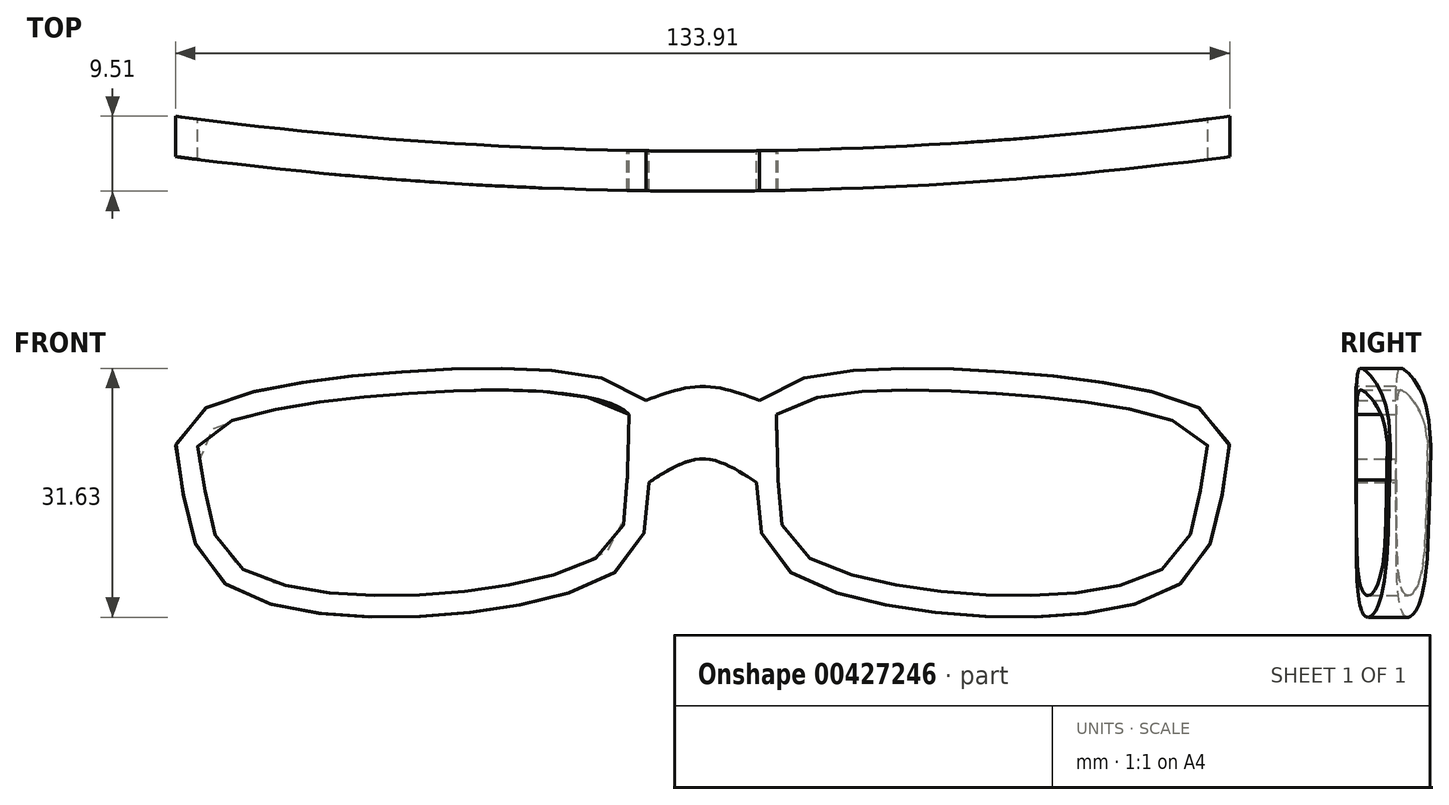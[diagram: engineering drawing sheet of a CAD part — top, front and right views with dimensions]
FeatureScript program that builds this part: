
annotation { "Feature Type Name" : "Feature", "Feature Type Description" : "" }
export const myFeature = defineFeature(function(context is Context, id is Id, definition is map)
    precondition{}
    {
        {
            var Q0;
            Q0=qCreatedBy(makeId("Front.planeOp"),FACE);
            var sketch = newSketch(context, id + "F0", { "sketchPlane" : qUnion([Q0])});
            skFitSpline(sketch, "E0", {"points": [v(-85.04, 21.14) * mm, v(-85.04, 29.55) * mm, v(-57.42, 36.35) * mm, v(-26.2, 32.75) * mm, v(-25.8, 22.34) * mm, v(-29.8, 11.13) * mm, v(-77.83, 8.33) * mm, v(-85.04, 21.14) * mm]});
            skLineSegment(sketch, "E1", {"start": v(-19, 51.16) * mm, "end": v(-19, -19.28) * mm, "construction": true});
            skFitSpline(sketch, "E2.MirrorC", {"points": [v(47.04, 21.14) * mm, v(47.04, 29.55) * mm, v(19.43, 36.35) * mm, v(-11.8, 32.75) * mm, v(-12.2, 22.34) * mm, v(-8.19, 11.13) * mm, v(39.84, 8.33) * mm, v(47.04, 21.14) * mm]});
            skFitSpline(sketch, "E3", {"points": [v(-26.2, 32.75) * mm, v(-19, 34.53) * mm, v(-11.8, 32.75) * mm], "startDerivative": vector(14.4, 5.34) * mm, "endDerivative": vector(14.4, -5.34) * mm});
            skFitSpline(sketch, "E4", {"points": [v(-25.8, 22.34) * mm, v(-19, 25.32) * mm, v(-12.2, 22.34) * mm], "startDerivative": vector(13.6, 8.94) * mm, "endDerivative": vector(13.6, -8.94) * mm});
            skSolve(sketch);
        }
        {
            var Q0;
            {var subQ0=sQuery(id+"F0.wireOp",EDGE,"E0");var subQ1=makeQuery(id+"F0.imprint","INTERSECT",VERTEX,{"derivedFrom":[subQ0,sQuery(id+"F0.wireOp",EDGE,"E3")]});Q0=makeQuery(id+"F0.imprint","IMPRINT",FACE,{"disambiguationData":[TD([[makeQuery(id+"F0.imprint","IMPRINT",EDGE,{"disambiguationData":[TD([[subQ1,-1.0]])],"derivedFrom":subQ0}),-1.0]])]});}
            var Q1;
            {var subQ0=sQuery(id+"F0.wireOp",EDGE,"E3");Q1=makeQuery(id+"F0.imprint","IMPRINT",FACE,{"disambiguationData":[TD([[makeQuery(id+"F0.imprint","IMPRINT",EDGE,{"derivedFrom":subQ0}),-1.0]])]});}
            var Q2;
            {var subQ0=sQuery(id+"F0.wireOp",EDGE,"E2.MirrorC");var subQ1=makeQuery(id+"F0.imprint","INTERSECT",VERTEX,{"derivedFrom":[subQ0,sQuery(id+"F0.wireOp",EDGE,"E3")]});Q2=makeQuery(id+"F0.imprint","IMPRINT",FACE,{"disambiguationData":[TD([[makeQuery(id+"F0.imprint","IMPRINT",EDGE,{"disambiguationData":[TD([[subQ1,-1.0]])],"derivedFrom":subQ0}),1.0]])]});}
            extrude(context, id + "F1", {"entities" : qUnion([Q0, Q1, Q2]), "depth" : 50.8 * mm});
        }
        {
            var Q0;
            Q0=qCreatedBy(makeId("Top.planeOp"),FACE);
            var sketch = newSketch(context, id + "F2", { "sketchPlane" : qUnion([Q0])});
            skPoint(sketch, "E5.0", {"position": v(-19, 0) * mm});
            skLineSegment(sketch, "E6", {"start": v(-85.95, -425) * mm, "end": v(-85.95, -30.52) * mm, "construction": true});
            skLineSegment(sketch, "E7", {"start": v(47.95, 0) * mm, "end": v(47.95, -25.4) * mm, "construction": true});
            skArc(sketch, "E8", {"start": v(-85.95, -25.4) * mm, "mid": v(-19, -29.83) * mm, "end": v(47.95, -25.4) * mm});
            skArc(sketch, "E9.0", {"start": v(-85.95, -30.52) * mm, "mid": v(-19, -34.91) * mm, "end": v(47.95, -30.52) * mm});
            skLineSegment(sketch, "E10", {"start": v(-85.95, -50.8) * mm, "end": v(-85.95, -30.52) * mm});
            skLineSegment(sketch, "E11", {"start": v(47.95, 0) * mm, "end": v(47.95, -25.4) * mm});
            skLineSegment(sketch, "E12", {"start": v(-85.95, -50.8) * mm, "end": v(47.95, -50.8) * mm});
            skLineSegment(sketch, "E13", {"start": v(47.95, 0) * mm, "end": v(-85.95, 0) * mm});
            skLineSegment(sketch, "E14.trimOffspring", {"start": v(47.95, -30.52) * mm, "end": v(47.95, -50.8) * mm, "construction": true});
            skLineSegment(sketch, "E15.trimOffspring", {"start": v(47.95, -30.52) * mm, "end": v(47.95, -50.8) * mm});
            skLineSegment(sketch, "E16.trimOffspring", {"start": v(-85.95, -25.4) * mm, "end": v(-85.95, 374.2) * mm, "construction": true});
            skLineSegment(sketch, "E17.trimOffspring", {"start": v(-85.95, -25.4) * mm, "end": v(-85.95, 0) * mm});
            skSolve(sketch);
        }
        {
            var Q0;
            Q0 = qSketchRegion(id + "F2", true);
            extrude(context, id + "F3", {"entities" : qUnion([Q0]), "operationType" : NewBodyOperationType.REMOVE, "depth" : 127 * mm});
        }
        {
            var Q0;
            Q0=qCreatedBy(makeId("Front.planeOp"),FACE);
            var sketch = newSketch(context, id + "F4", { "sketchPlane" : qUnion([Q0])});
            skFitSpline(sketch, "E18.0.0", {"points": [v(-26.2, 32.75) * mm, v(-26.45, 33.05) * mm, v(-27.02, 33.57) * mm, v(-27.83, 34.1) * mm, v(-28.52, 34.46) * mm, v(-29.22, 34.78) * mm, v(-30.12, 35.12) * mm, v(-31.22, 35.45) * mm, v(-32.34, 35.73) * mm, v(-33.47, 35.96) * mm, v(-34.99, 36.22) * mm, v(-36.89, 36.46) * mm, v(-39.93, 36.71) * mm, v(-43.73, 36.85) * mm, v(-48.3, 36.82) * mm, v(-52.88, 36.64) * mm, v(-57.45, 36.36) * mm, v(-62, 36) * mm, v(-65.8, 35.6) * mm, v(-68.8, 35.2) * mm, v(-71.06, 34.86) * mm, v(-73.31, 34.46) * mm, v(-75.55, 33.98) * mm, v(-77.76, 33.42) * mm, v(-79.57, 32.85) * mm, v(-80.99, 32.3) * mm, v(-82.04, 31.83) * mm, v(-83.05, 31.28) * mm, v(-83.83, 30.74) * mm, v(-84.42, 30.24) * mm, v(-84.83, 29.82) * mm, v(-85.18, 29.37) * mm, v(-85.47, 28.86) * mm, v(-85.7, 28.33) * mm, v(-85.84, 27.77) * mm, v(-85.93, 27.2) * mm, v(-85.96, 26.43) * mm, v(-85.9, 25.47) * mm, v(-85.71, 24.32) * mm, v(-85.48, 23.19) * mm, v(-85.23, 22.06) * mm, v(-84.99, 20.93) * mm, v(-84.78, 19.8) * mm, v(-84.56, 18.65) * mm, v(-84.25, 17.14) * mm, v(-83.87, 15.65) * mm, v(-83.32, 14.19) * mm, v(-82.83, 13.14) * mm, v(-82.25, 12.16) * mm, v(-81.56, 11.23) * mm, v(-80.77, 10.37) * mm, v(-79.9, 9.62) * mm, v(-78.96, 8.96) * mm, v(-77.96, 8.38) * mm, v(-76.91, 7.89) * mm, v(-75.84, 7.46) * mm, v(-74.76, 7.1) * mm, v(-73.3, 6.68) * mm, v(-71.44, 6.25) * mm, v(-69.55, 5.93) * mm, v(-68.03, 5.72) * mm, v(-65.75, 5.46) * mm, v(-62.33, 5.22) * mm, v(-57.79, 5.17) * mm, v(-53.24, 5.34) * mm, v(-48.7, 5.73) * mm, v(-44.93, 6.25) * mm, v(-41.9, 6.8) * mm, v(-39.65, 7.28) * mm, v(-37.42, 7.85) * mm, v(-35.21, 8.53) * mm, v(-33.42, 9.2) * mm, v(-32.03, 9.83) * mm, v(-31.01, 10.36) * mm, v(-30.19, 10.86) * mm, v(-29.55, 11.31) * mm, v(-28.95, 11.79) * mm, v(-28.4, 12.32) * mm, v(-27.9, 12.9) * mm, v(-27.56, 13.38) * mm, v(-27.25, 13.87) * mm, v(-26.9, 14.55) * mm, v(-26.56, 15.44) * mm, v(-26.28, 16.58) * mm, v(-26.06, 18.1) * mm, v(-25.95, 20.03) * mm, v(-25.88, 21.57) * mm, v(-25.8, 22.34) * mm]});
            skFitSpline(sketch, "E18.0.1", {"points": [v(-25.8, 22.34) * mm, v(-25.28, 22.68) * mm, v(-24.23, 23.37) * mm, v(-22.89, 24.16) * mm, v(-21.9, 24.63) * mm, v(-21.32, 24.86) * mm, v(-20.72, 25.07) * mm, v(-19.96, 25.26) * mm, v(-19.18, 25.33) * mm, v(-18.54, 25.3) * mm, v(-17.92, 25.23) * mm, v(-17.16, 25.04) * mm, v(-16.26, 24.71) * mm, v(-15.12, 24.17) * mm, v(-13.77, 23.38) * mm, v(-12.72, 22.69) * mm, v(-12.2, 22.34) * mm]});
            skFitSpline(sketch, "E18.0.2", {"points": [v(-12.2, 22.34) * mm, v(-12.12, 21.57) * mm, v(-12.04, 20.03) * mm, v(-11.94, 18.1) * mm, v(-11.71, 16.58) * mm, v(-11.44, 15.44) * mm, v(-11.1, 14.55) * mm, v(-10.74, 13.87) * mm, v(-10.44, 13.38) * mm, v(-10.1, 12.9) * mm, v(-9.6, 12.32) * mm, v(-9.04, 11.79) * mm, v(-8.44, 11.31) * mm, v(-7.8, 10.86) * mm, v(-6.98, 10.36) * mm, v(-5.96, 9.83) * mm, v(-4.57, 9.2) * mm, v(-2.78, 8.53) * mm, v(-0.57, 7.85) * mm, v(1.66, 7.28) * mm, v(3.91, 6.8) * mm, v(6.94, 6.25) * mm, v(10.71, 5.73) * mm, v(15.25, 5.34) * mm, v(19.8, 5.17) * mm, v(24.34, 5.22) * mm, v(27.76, 5.46) * mm, v(30.04, 5.72) * mm, v(31.56, 5.93) * mm, v(33.44, 6.25) * mm, v(35.3, 6.68) * mm, v(36.77, 7.1) * mm, v(37.85, 7.46) * mm, v(38.92, 7.89) * mm, v(39.97, 8.38) * mm, v(40.97, 8.96) * mm, v(41.9, 9.62) * mm, v(42.77, 10.37) * mm, v(43.57, 11.23) * mm, v(44.26, 12.16) * mm, v(44.84, 13.14) * mm, v(45.33, 14.19) * mm, v(45.87, 15.65) * mm, v(46.26, 17.14) * mm, v(46.57, 18.65) * mm, v(46.78, 19.8) * mm, v(47, 20.93) * mm, v(47.24, 22.06) * mm, v(47.49, 23.19) * mm, v(47.72, 24.32) * mm, v(47.9, 25.47) * mm, v(47.97, 26.43) * mm, v(47.93, 27.2) * mm, v(47.85, 27.77) * mm, v(47.7, 28.33) * mm, v(47.48, 28.86) * mm, v(47.18, 29.37) * mm, v(46.83, 29.82) * mm, v(46.43, 30.24) * mm, v(45.84, 30.74) * mm, v(45.05, 31.28) * mm, v(44.04, 31.83) * mm, v(43, 32.3) * mm, v(41.58, 32.85) * mm, v(39.77, 33.42) * mm, v(37.56, 33.98) * mm, v(35.32, 34.46) * mm, v(33.07, 34.86) * mm, v(30.82, 35.2) * mm, v(27.8, 35.6) * mm, v(24.01, 36) * mm, v(19.46, 36.36) * mm, v(14.89, 36.64) * mm, v(10.31, 36.82) * mm, v(5.74, 36.85) * mm, v(1.94, 36.71) * mm, v(-1.1, 36.46) * mm, v(-3, 36.22) * mm, v(-4.52, 35.96) * mm, v(-5.66, 35.73) * mm, v(-6.77, 35.45) * mm, v(-7.87, 35.12) * mm, v(-8.77, 34.78) * mm, v(-9.47, 34.46) * mm, v(-10.16, 34.1) * mm, v(-10.97, 33.57) * mm, v(-11.54, 33.05) * mm, v(-11.8, 32.75) * mm]});
            skFitSpline(sketch, "E18.0.3", {"points": [v(-11.8, 32.75) * mm, v(-12.38, 32.96) * mm, v(-13.55, 33.4) * mm, v(-15.32, 33.98) * mm, v(-17.15, 34.4) * mm, v(-18.68, 34.56) * mm, v(-19.92, 34.5) * mm, v(-21.17, 34.33) * mm, v(-22.68, 33.97) * mm, v(-24.45, 33.4) * mm, v(-25.62, 32.96) * mm, v(-26.2, 32.75) * mm]});
            skFitSpline(sketch, "E19.0", {"points": [v(-9.41, 22.62) * mm, v(-9.33, 21.76) * mm, v(-9.25, 20.13) * mm, v(-9.15, 18.34) * mm, v(-8.96, 17.1) * mm, v(-8.76, 16.27) * mm, v(-8.49, 15.56) * mm, v(-8.19, 15.04) * mm, v(-7.9, 14.64) * mm, v(-7.57, 14.26) * mm, v(-7.2, 13.9) * mm, v(-6.76, 13.55) * mm, v(-6.28, 13.2) * mm, v(-5.62, 12.8) * mm, v(-4.75, 12.35) * mm, v(-3.52, 11.8) * mm, v(-1.88, 11.18) * mm, v(0.18, 10.55) * mm, v(3, 9.82) * mm, v(6.63, 9.11) * mm, v(11.02, 8.51) * mm, v(15.43, 8.13) * mm, v(19.83, 7.96) * mm, v(24.24, 8.01) * mm, v(27.88, 8.26) * mm, v(30.77, 8.63) * mm, v(32.9, 9) * mm, v(34.96, 9.47) * mm, v(36.6, 9.97) * mm, v(37.66, 10.4) * mm, v(38.25, 10.66) * mm, v(38.81, 10.94) * mm, v(39.47, 11.32) * mm, v(40.18, 11.83) * mm, v(40.83, 12.38) * mm, v(41.42, 13.02) * mm, v(41.92, 13.7) * mm, v(42.36, 14.45) * mm, v(42.75, 15.26) * mm, v(43.2, 16.46) * mm, v(43.54, 17.77) * mm, v(43.8, 19) * mm, v(43.93, 19.74) * mm, v(44.04, 20.3) * mm, v(44.14, 20.88) * mm, v(44.26, 21.47) * mm, v(44.38, 22.07) * mm, v(44.55, 22.85) * mm, v(44.76, 23.79) * mm, v(44.98, 24.84) * mm, v(45.13, 25.8) * mm, v(45.17, 26.5) * mm, v(45.15, 26.93) * mm, v(45.1, 27.22) * mm, v(45.05, 27.4) * mm, v(45, 27.53) * mm, v(44.95, 27.65) * mm, v(44.88, 27.77) * mm, v(44.8, 27.89) * mm, v(44.7, 28.01) * mm, v(44.52, 28.2) * mm, v(44.17, 28.5) * mm, v(43.61, 28.88) * mm, v(42.8, 29.32) * mm, v(41.92, 29.72) * mm, v(40.67, 30.2) * mm, v(39.01, 30.73) * mm, v(36.93, 31.26) * mm, v(34.8, 31.71) * mm, v(32.62, 32.1) * mm, v(30.43, 32.43) * mm, v(27.48, 32.82) * mm, v(23.76, 33.21) * mm, v(19.26, 33.58) * mm, v(14.74, 33.85) * mm, v(10.25, 34.02) * mm, v(5.77, 34.05) * mm, v(2.09, 33.92) * mm, v(-0.82, 33.68) * mm, v(-2.6, 33.45) * mm, v(-4.01, 33.22) * mm, v(-5.04, 33) * mm, v(-6.03, 32.76) * mm, v(-6.98, 32.47) * mm, v(-7.71, 32.2) * mm, v(-8.25, 31.95) * mm, v(-8.63, 31.75) * mm, v(-8.96, 31.55) * mm, v(-9.25, 31.34) * mm, v(-9.48, 31.14) * mm, v(-9.6, 31.02) * mm, v(-9.65, 30.96) * mm]});
            skFitSpline(sketch, "E20.0", {"points": [v(-28.35, 30.96) * mm, v(-28.4, 31.02) * mm, v(-28.51, 31.14) * mm, v(-28.75, 31.34) * mm, v(-29.03, 31.55) * mm, v(-29.37, 31.75) * mm, v(-29.75, 31.95) * mm, v(-30.28, 32.2) * mm, v(-31.01, 32.47) * mm, v(-31.96, 32.76) * mm, v(-32.95, 33) * mm, v(-33.98, 33.22) * mm, v(-35.39, 33.45) * mm, v(-37.17, 33.68) * mm, v(-40.08, 33.92) * mm, v(-43.77, 34.05) * mm, v(-48.24, 34.02) * mm, v(-52.74, 33.85) * mm, v(-57.25, 33.58) * mm, v(-61.75, 33.21) * mm, v(-65.47, 32.82) * mm, v(-68.42, 32.43) * mm, v(-70.61, 32.1) * mm, v(-72.78, 31.71) * mm, v(-74.93, 31.26) * mm, v(-77, 30.73) * mm, v(-78.66, 30.2) * mm, v(-79.91, 29.72) * mm, v(-80.8, 29.32) * mm, v(-81.6, 28.88) * mm, v(-82.16, 28.5) * mm, v(-82.51, 28.2) * mm, v(-82.69, 28.01) * mm, v(-82.79, 27.89) * mm, v(-82.87, 27.77) * mm, v(-82.94, 27.65) * mm, v(-83, 27.53) * mm, v(-83.05, 27.4) * mm, v(-83.1, 27.22) * mm, v(-83.14, 26.93) * mm, v(-83.16, 26.5) * mm, v(-83.12, 25.8) * mm, v(-82.97, 24.84) * mm, v(-82.75, 23.79) * mm, v(-82.54, 22.85) * mm, v(-82.37, 22.07) * mm, v(-82.25, 21.47) * mm, v(-82.14, 20.88) * mm, v(-82.03, 20.3) * mm, v(-81.92, 19.74) * mm, v(-81.78, 19) * mm, v(-81.53, 17.77) * mm, v(-81.19, 16.46) * mm, v(-80.74, 15.26) * mm, v(-80.36, 14.45) * mm, v(-79.91, 13.7) * mm, v(-79.41, 13.02) * mm, v(-78.82, 12.38) * mm, v(-78.18, 11.83) * mm, v(-77.46, 11.32) * mm, v(-76.8, 10.94) * mm, v(-76.24, 10.66) * mm, v(-75.65, 10.4) * mm, v(-74.58, 9.97) * mm, v(-72.95, 9.47) * mm, v(-70.9, 9) * mm, v(-68.77, 8.63) * mm, v(-65.87, 8.26) * mm, v(-62.23, 8.01) * mm, v(-57.83, 7.96) * mm, v(-53.42, 8.13) * mm, v(-49.01, 8.51) * mm, v(-44.63, 9.11) * mm, v(-41, 9.82) * mm, v(-38.18, 10.55) * mm, v(-36.1, 11.18) * mm, v(-34.47, 11.8) * mm, v(-33.24, 12.35) * mm, v(-32.37, 12.8) * mm, v(-31.71, 13.2) * mm, v(-31.23, 13.55) * mm, v(-30.8, 13.9) * mm, v(-30.42, 14.26) * mm, v(-30.1, 14.64) * mm, v(-29.8, 15.04) * mm, v(-29.5, 15.56) * mm, v(-29.23, 16.27) * mm, v(-29.03, 17.1) * mm, v(-28.84, 18.34) * mm, v(-28.74, 20.13) * mm, v(-28.67, 21.76) * mm, v(-28.58, 22.62) * mm]});
            skFitSpline(sketch, "E21", {"points": [v(-28.35, 30.96) * mm, v(-28.58, 22.62) * mm], "startDerivative": vector(-0.24, -8.34) * mm, "endDerivative": vector(-0.24, -8.34) * mm});
            skFitSpline(sketch, "E22", {"points": [v(-9.41, 22.62) * mm, v(-9.65, 30.96) * mm], "startDerivative": vector(-0.24, 8.34) * mm, "endDerivative": vector(-0.24, 8.34) * mm});
            skSolve(sketch);
        }
        {
            var Q0;
            Q0=makeQuery(id+"F4.imprint","IMPRINT",FACE,{"disambiguationData":[TD([[makeQuery(id+"F4.imprint","IMPRINT",EDGE,{"derivedFrom":sQuery(id+"F4.wireOp",EDGE,"E19.0")}),1.0]])]});
            var Q1;
            Q1=makeQuery(id+"F4.imprint","IMPRINT",FACE,{"disambiguationData":[TD([[makeQuery(id+"F4.imprint","IMPRINT",EDGE,{"derivedFrom":sQuery(id+"F4.wireOp",EDGE,"E20.0")}),1.0]])]});
            extrude(context, id + "F5", {"entities" : qUnion([Q0, Q1]), "operationType" : NewBodyOperationType.REMOVE, "depth" : 50.8 * mm});
        }
    });
